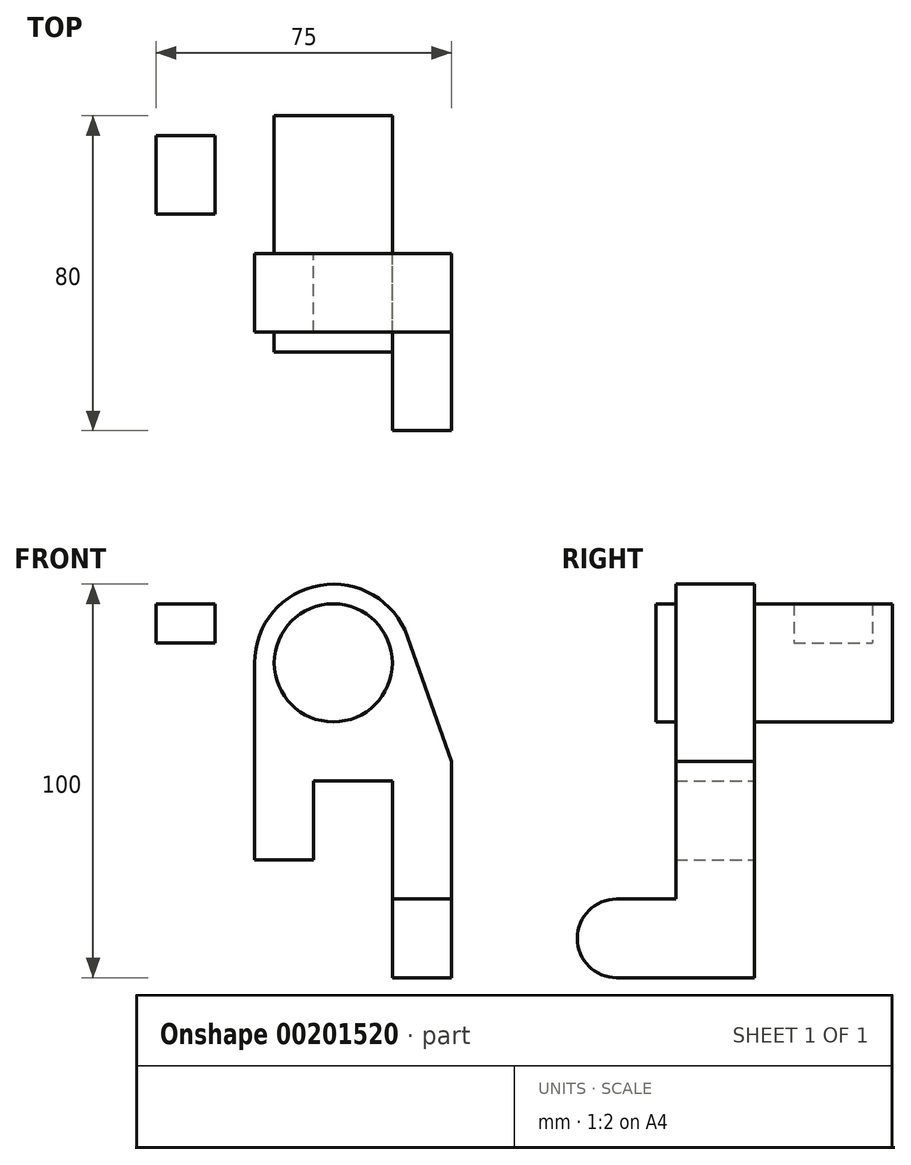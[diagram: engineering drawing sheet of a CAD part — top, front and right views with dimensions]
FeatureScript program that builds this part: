
annotation { "Feature Type Name" : "Feature", "Feature Type Description" : "" }
export const myFeature = defineFeature(function(context is Context, id is Id, definition is map)
    precondition{}
    {
        {
            var Q0;
            Q0=qCreatedBy(makeId("Front.planeOp"),FACE);
            var sketch = newSketch(context, id + "F0", { "sketchPlane" : qUnion([Q0])});
            skCircle(sketch, "E0", {"center": v(0, 0) * mm, "radius": 15 * mm});
            skCircle(sketch, "E1", {"center": v(0, 0) * mm, "radius": 20 * mm});
            skLineSegment(sketch, "E2", {"start": v(-20, 0) * mm, "end": v(-20, -50) * mm});
            skLineSegment(sketch, "E3", {"start": v(-20, -50) * mm, "end": v(-5, -50) * mm});
            skLineSegment(sketch, "E4", {"start": v(-5, -50) * mm, "end": v(-5, -30) * mm});
            skLineSegment(sketch, "E5", {"start": v(-5, -30) * mm, "end": v(15, -30) * mm});
            skLineSegment(sketch, "E6", {"start": v(15, -30) * mm, "end": v(15, -80) * mm});
            skLineSegment(sketch, "E7", {"start": v(15, -80) * mm, "end": v(30, -80) * mm});
            skLineSegment(sketch, "E8", {"start": v(30, -80) * mm, "end": v(30, -25) * mm});
            skLineSegment(sketch, "E9", {"start": v(30, -25) * mm, "end": v(18.87, 6.64) * mm});
            skLineSegment(sketch, "E10", {"start": v(15, -60) * mm, "end": v(30, -60) * mm});
            skSolve(sketch);
        }
        {
            var Q0;
            Q0=qSketchRegion(id+"F0",true);
            extrude(context, id + "F1", {"entities" : qUnion([Q0]), "depth" : 20 * mm});
        }
        {
            var Q0;
            {var subQ0=sQuery(id+"F0.wireOp",EDGE,"E7");Q0=makeQuery(id+"F0.imprint","IMPRINT",FACE,{"disambiguationData":[TD([[makeQuery(id+"F0.imprint","IMPRINT",EDGE,{"derivedFrom":subQ0}),1.0]])]});}
            extrude(context, id + "F2", {"entities" : qUnion([Q0]), "operationType" : NewBodyOperationType.ADD, "depth" : (25 + 20) * mm});
        }
        {
            var Q0;
            Q0=makeQuery(id+"F0.imprint","IMPRINT",FACE,{"disambiguationData":[TD([[makeQuery(id+"F0.imprint","IMPRINT",EDGE,{"derivedFrom":sQuery(id+"F0.wireOp",EDGE,"E0")}),1.0]])]});
            extrude(context, id + "F3", {"entities" : qUnion([Q0]), "operationType" : NewBodyOperationType.ADD, "depth" : 25 * mm, "hasSecondDirection" : true, "secondDirectionOppositeDirection" : true, "secondDirectionDepth" : (60 - 25) * mm});
        }
        {
            var Q0;
            Q0=makeQuery(id+"F2.opExtrude","CAP_EDGE",EDGE,{"disambiguationData":[OSD([sQuery(id+"F0.wireOp",EDGE,"E10")])],"isStart":false});
            var Q1;
            Q1=makeQuery(id+"F2.opExtrude","CAP_EDGE",EDGE,{"disambiguationData":[OSD([sQuery(id+"F0.wireOp",EDGE,"E7")])],"isStart":false});
            fillet(context, id + "F4", {"entities" : qUnion([Q0, Q1]), "radius" : 10 * mm, "tangentPropagation" : true, "allowEdgeOverflow" : false});
        }
        {
            var Q0;
            Q0=makeQuery(id+"F3.opExtrude","CAP_FACE",FACE,{"disambiguationData":[OSD([sQuery(id+"F0.wireOp",EDGE,"E0")])],"isStart":true});
            var sketch = newSketch(context, id + "F5", { "sketchPlane" : qUnion([Q0])});
            skLineSegment(sketch, "E11.bottom", {"start": v(0, 15) * mm, "end": v(45, 15) * mm});
            skLineSegment(sketch, "E11.top", {"start": v(0, -15) * mm, "end": v(45, -15) * mm});
            skLineSegment(sketch, "E11.left", {"start": v(0, 15) * mm, "end": v(0, -15) * mm});
            skLineSegment(sketch, "E11.right", {"start": v(45, 15) * mm, "end": v(45, -15) * mm});
            skLineSegment(sketch, "E12.bottom", {"start": v(45, 15) * mm, "end": v(30, 15) * mm});
            skLineSegment(sketch, "E12.top", {"start": v(45, 5) * mm, "end": v(30, 5) * mm});
            skLineSegment(sketch, "E12.left", {"start": v(45, 15) * mm, "end": v(45, 5) * mm});
            skLineSegment(sketch, "E12.right", {"start": v(30, 15) * mm, "end": v(30, 5) * mm});
            skCircle(sketch, "E13.0", {"center": v(0, 0) * mm, "radius": 15 * mm});
            skSolve(sketch);
        }
        {
            var Q0;
            {var subQ1=sQuery(id+"F5.wireOp",EDGE,"E11.bottom");Q0=makeQuery(id+"F5.imprint","IMPRINT",FACE,{"disambiguationData":[TD([[makeQuery(id+"F5.imprint","IMPRINT",EDGE,{"derivedFrom":subQ1}),-1.0]])]});}
            extrude(context, id + "F6", {"entities" : qUnion([Q0]), "operationType" : NewBodyOperationType.ADD, "oppositeDirection" : true, "depth" : 25 * mm});
        }
        {
            var Q0;
            {var subQ2=sQuery(id+"F5.wireOp",EDGE,"E11.bottom");Q0=makeQuery(id+"F5.imprint","IMPRINT",FACE,{"disambiguationData":[TD([[makeQuery(id+"F5.imprint","IMPRINT",EDGE,{"derivedFrom":subQ2}),-1.0]])]});}
            extrude(context, id + "F7", {"entities" : qUnion([Q0]), "operationType" : NewBodyOperationType.REMOVE, "oppositeDirection" : true, "depth" : 5 * mm});
        }
    });
